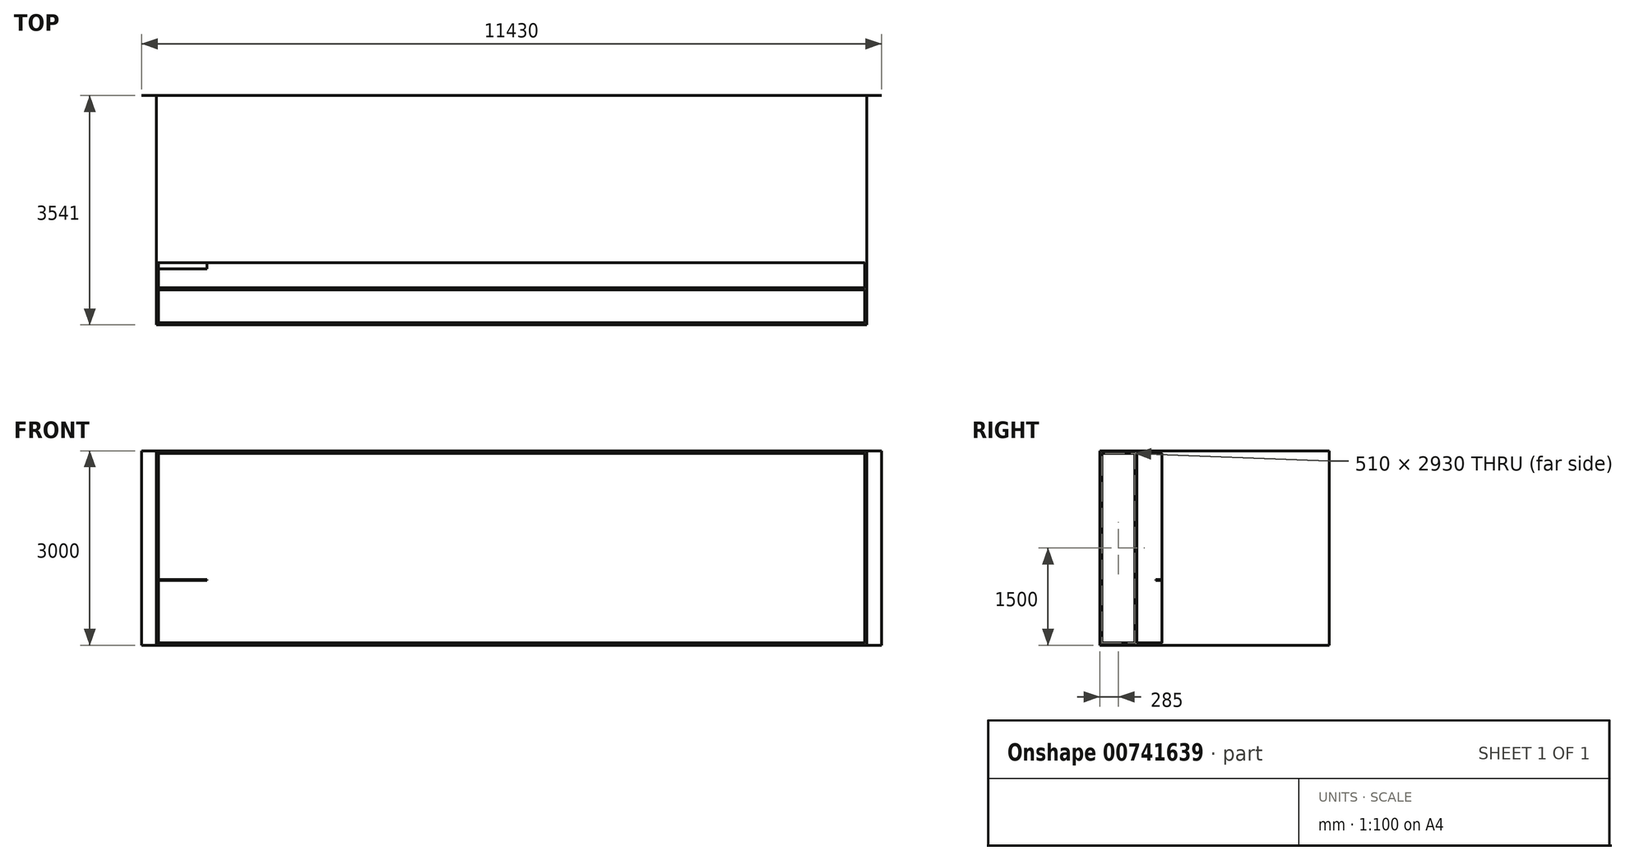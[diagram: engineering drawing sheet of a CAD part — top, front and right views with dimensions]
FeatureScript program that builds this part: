
annotation { "Feature Type Name" : "Feature", "Feature Type Description" : "" }
export const myFeature = defineFeature(function(context is Context, id is Id, definition is map)
    precondition{}
    {
        {
            var Q0;
            Q0=qCreatedBy(makeId("Front.planeOp"),FACE);
            var sketch = newSketch(context, id + "F0", { "sketchPlane" : qUnion([Q0])});
            skLineSegment(sketch, "E0.bottom", {"start": v(-5485, 1500) * mm, "end": v(5485, 1500) * mm});
            skLineSegment(sketch, "E0.top", {"start": v(-5485, -1500) * mm, "end": v(5485, -1500) * mm});
            skLineSegment(sketch, "E0.left", {"start": v(-5485, 1500) * mm, "end": v(-5485, -1500) * mm});
            skLineSegment(sketch, "E0.right", {"start": v(5485, 1500) * mm, "end": v(5485, -1500) * mm});
            skPoint(sketch, "E0.middle", {"position": v(0, 0) * mm});
            skSolve(sketch);
        }
        {
            var Q0;
            Q0=qSketchRegion(id+"F0",true);
            extrude(context, id + "F1", {"entities" : qUnion([Q0]), "depth" : 2580 * mm});
        }
        {
            var Q0;
            Q0=makeQuery(id+"F1.opExtrude","SWEPT_FACE",FACE,{"disambiguationData":[OSD([sQuery(id+"F0.wireOp",EDGE,"E0.left")])]});
            var sketch = newSketch(context, id + "F2", { "sketchPlane" : qUnion([Q0])});
            skPoint(sketch, "E1.middle", {"position": v(0, 0) * mm});
            skLineSegment(sketch, "E2", {"start": v(2580, 1500) * mm, "end": v(3540, 1500) * mm});
            skLineSegment(sketch, "E3", {"start": v(2580, -1500) * mm, "end": v(3540, -1500) * mm});
            skLineSegment(sketch, "E4", {"start": v(3540, 1500) * mm, "end": v(3540, -1500) * mm});
            skLineSegment(sketch, "E5", {"start": v(3510, 1465) * mm, "end": v(3510, -1465) * mm});
            skLineSegment(sketch, "E6", {"start": v(3540, 1465) * mm, "end": v(3540, -1465) * mm});
            skLineSegment(sketch, "E7", {"start": v(3000, -1465) * mm, "end": v(3000, 1465) * mm});
            skLineSegment(sketch, "E8", {"start": v(2970, 1465) * mm, "end": v(2970, -1465) * mm});
            skLineSegment(sketch, "E9", {"start": v(3510, 1465) * mm, "end": v(2580, 1465) * mm});
            skLineSegment(sketch, "E10", {"start": v(3510, -1465) * mm, "end": v(2580, -1465) * mm});
            skLineSegment(sketch, "E11", {"start": v(2580, 1465) * mm, "end": v(2580, 1500) * mm});
            skLineSegment(sketch, "E12", {"start": v(2580, -1465) * mm, "end": v(2580, -1500) * mm});
            skLineSegment(sketch, "E13", {"start": v(2580, -1500) * mm, "end": v(2580, -500) * mm, "construction": true});
            skLineSegment(sketch, "E14", {"start": v(2580, -500) * mm, "end": v(2679.7, -500) * mm});
            skLineSegment(sketch, "E15", {"start": v(2679.7, -500) * mm, "end": v(2679.7, -487.96) * mm});
            skLineSegment(sketch, "E16", {"start": v(2679.7, -487.96) * mm, "end": v(2580, -487.96) * mm});
            skLineSegment(sketch, "E17", {"start": v(2580, -487.96) * mm, "end": v(2580, -500) * mm});
            skSolve(sketch);
        }
        {
            var Q0;
            {var subQ0=sQuery(id+"F2.wireOp",EDGE,"E4");Q0=makeQuery(id+"F2.imprint","IMPRINT",FACE,{"disambiguationData":[TD([[makeQuery(id+"F2.imprint","IMPRINT",EDGE,{"derivedFrom":subQ0}),-1.0]])]});}
            var Q1;
            {var subQ0=sQuery(id+"F2.wireOp",EDGE,"2suLI4y7-gJnx-pfue-NYUh-xxraCEmb6OIi");Q1=makeQuery(id+"F2.imprint","IMPRINT",FACE,{"disambiguationData":[TD([[makeQuery(id+"F2.imprint","IMPRINT",EDGE,{"derivedFrom":subQ0}),-1.0]])]});}
            var Q2;
            {var subQ0=sQuery(id+"F2.wireOp",EDGE,"E7");Q2=makeQuery(id+"F2.imprint","IMPRINT",FACE,{"disambiguationData":[TD([[makeQuery(id+"F2.imprint","IMPRINT",EDGE,{"derivedFrom":subQ0}),1.0]])]});}
            extrude(context, id + "F3", {"entities" : qUnion([Q0, Q1, Q2]), "oppositeDirection" : true, "depth" : 30 * mm});
        }
        {
            var Q0;
            Q0=makeQuery(id+"F3.opExtrude","CAP_FACE",FACE,{"disambiguationData":[OSD([sQuery(id+"F2.wireOp",EDGE,"E2"),sQuery(id+"F2.wireOp",EDGE,"E3"),sQuery(id+"F2.wireOp",EDGE,"E4"),sQuery(id+"F2.wireOp",EDGE,"E5"),sQuery(id+"F2.wireOp",EDGE,"E6"),sQuery(id+"F2.wireOp",EDGE,"E9"),sQuery(id+"F2.wireOp",EDGE,"E10"),sQuery(id+"F2.wireOp",EDGE,"E11"),sQuery(id+"F2.wireOp",EDGE,"E12")])],"isStart":true});
            var sketch = newSketch(context, id + "F4", { "sketchPlane" : qUnion([Q0])});
            skLineSegment(sketch, "E18.bottom", {"start": v(3000, 1465) * mm, "end": v(2970, 1465) * mm});
            skLineSegment(sketch, "E18.top", {"start": v(3000, 1500) * mm, "end": v(2970, 1500) * mm});
            skLineSegment(sketch, "E18.left", {"start": v(3000, 1465) * mm, "end": v(3000, 1500) * mm});
            skLineSegment(sketch, "E18.right", {"start": v(2970, 1465) * mm, "end": v(2970, 1500) * mm});
            skLineSegment(sketch, "E19.bottom", {"start": v(2970, -1465) * mm, "end": v(3000, -1465) * mm});
            skLineSegment(sketch, "E19.top", {"start": v(2970, -1500) * mm, "end": v(3000, -1500) * mm});
            skLineSegment(sketch, "E19.left", {"start": v(2970, -1465) * mm, "end": v(2970, -1500) * mm});
            skLineSegment(sketch, "E19.right", {"start": v(3000, -1465) * mm, "end": v(3000, -1500) * mm});
            skLineSegment(sketch, "E20.bottom", {"start": v(3540, -1500) * mm, "end": v(3510, -1500) * mm});
            skLineSegment(sketch, "E20.top", {"start": v(3540, -1465) * mm, "end": v(3510, -1465) * mm});
            skLineSegment(sketch, "E20.left", {"start": v(3540, -1500) * mm, "end": v(3540, -1465) * mm});
            skLineSegment(sketch, "E20.right", {"start": v(3510, -1500) * mm, "end": v(3510, -1465) * mm});
            skLineSegment(sketch, "E21.bottom", {"start": v(3510, 1465) * mm, "end": v(3540, 1465) * mm});
            skLineSegment(sketch, "E21.top", {"start": v(3510, 1500) * mm, "end": v(3540, 1500) * mm});
            skLineSegment(sketch, "E21.left", {"start": v(3510, 1465) * mm, "end": v(3510, 1500) * mm});
            skLineSegment(sketch, "E21.right", {"start": v(3540, 1465) * mm, "end": v(3540, 1500) * mm});
            skSolve(sketch);
        }
        {
            var Q0;
            Q0=qSketchRegion(id+"F4",true);
            extrude(context, id + "F5", {"entities" : qUnion([Q0]), "oppositeDirection" : true, "depth" : 10940 * mm});
        }
        {
            var Q0;
            Q0=makeQuery(id+"F1.opExtrude","SWEPT_FACE",FACE,{"disambiguationData":[OSD([sQuery(id+"F0.wireOp",EDGE,"E0.right")])]});
            var sketch = newSketch(context, id + "F6", { "sketchPlane" : qUnion([Q0])});
            skLineSegment(sketch, "E22", {"start": v(-2580, -1500) * mm, "end": v(-3540, -1500) * mm});
            skLineSegment(sketch, "E23", {"start": v(-3540, -1500) * mm, "end": v(-3540, -1465) * mm});
            skLineSegment(sketch, "E24", {"start": v(-2580, -1465) * mm, "end": v(-2580, 1465) * mm});
            skLineSegment(sketch, "E25", {"start": v(-2580, 1465) * mm, "end": v(-2580, 1500) * mm});
            skLineSegment(sketch, "E26", {"start": v(-2580, 1500) * mm, "end": v(-3540, 1500) * mm});
            skLineSegment(sketch, "E27", {"start": v(-3540, 1500) * mm, "end": v(-3540, 1465) * mm});
            skLineSegment(sketch, "E28", {"start": v(-3510, -1465) * mm, "end": v(-3510, 1465) * mm});
            skLineSegment(sketch, "E29", {"start": v(-3540, 1465) * mm, "end": v(-3540, -1465) * mm});
            skLineSegment(sketch, "E30", {"start": v(-3510, -1465) * mm, "end": v(-3000, -1465) * mm});
            skLineSegment(sketch, "E31", {"start": v(-3000, -1465) * mm, "end": v(-3000, 1465) * mm});
            skLineSegment(sketch, "E32", {"start": v(-2969.84, 1465) * mm, "end": v(-2969.84, -1465) * mm});
            skLineSegment(sketch, "E33", {"start": v(-2969.84, 1465) * mm, "end": v(-2580, 1465) * mm});
            skLineSegment(sketch, "E34", {"start": v(-3510, 1465) * mm, "end": v(-3000, 1465) * mm});
            skLineSegment(sketch, "E35", {"start": v(-2969.84, -1465) * mm, "end": v(-2580, -1465) * mm});
            skSolve(sketch);
        }
        {
            var Q0;
            {var subQ0=sQuery(id+"F6.wireOp",EDGE,"E22");Q0=makeQuery(id+"F6.imprint","IMPRINT",FACE,{"disambiguationData":[TD([[makeQuery(id+"F6.imprint","IMPRINT",EDGE,{"derivedFrom":subQ0}),-1.0]])]});}
            extrude(context, id + "F7", {"entities" : qUnion([Q0]), "operationType" : NewBodyOperationType.ADD, "oppositeDirection" : true, "depth" : 30 * mm});
        }
        {
            var Q0;
            Q0=makeQuery(id+"F1.opExtrude","CAP_FACE",FACE,{"disambiguationData":[OSD([sQuery(id+"F0.wireOp",EDGE,"E0.bottom"),sQuery(id+"F0.wireOp",EDGE,"E0.top"),sQuery(id+"F0.wireOp",EDGE,"E0.left"),sQuery(id+"F0.wireOp",EDGE,"E0.right")])],"isStart":true});
            var sketch = newSketch(context, id + "F8", { "sketchPlane" : qUnion([Q0])});
            skLineSegment(sketch, "E36.bottom", {"start": v(5715, 1500) * mm, "end": v(-5715, 1500) * mm});
            skLineSegment(sketch, "E36.top", {"start": v(5715, -1500) * mm, "end": v(-5715, -1500) * mm});
            skLineSegment(sketch, "E36.left", {"start": v(5715, 1500) * mm, "end": v(5715, -1500) * mm});
            skLineSegment(sketch, "E36.right", {"start": v(-5715, 1500) * mm, "end": v(-5715, -1500) * mm});
            skPoint(sketch, "E36.middle", {"position": v(0, 0) * mm});
            skSolve(sketch);
        }
        {
            var Q0;
            Q0=qSketchRegion(id+"F8",true);
            extrude(context, id + "F9", {"entities" : qUnion([Q0]), "operationType" : NewBodyOperationType.ADD, "depth" : 1 * mm});
        }
        {
            var Q0;
            Q0=makeQuery(id+"F2.imprint","IMPRINT",FACE,{"disambiguationData":[TD([[makeQuery(id+"F2.imprint","IMPRINT",EDGE,{"derivedFrom":sQuery(id+"F2.wireOp",EDGE,"E14")}),1.0]])]});
            extrude(context, id + "F10", {"entities" : qUnion([Q0]), "operationType" : NewBodyOperationType.ADD, "oppositeDirection" : true, "depth" : 777 * mm});
        }
    });
